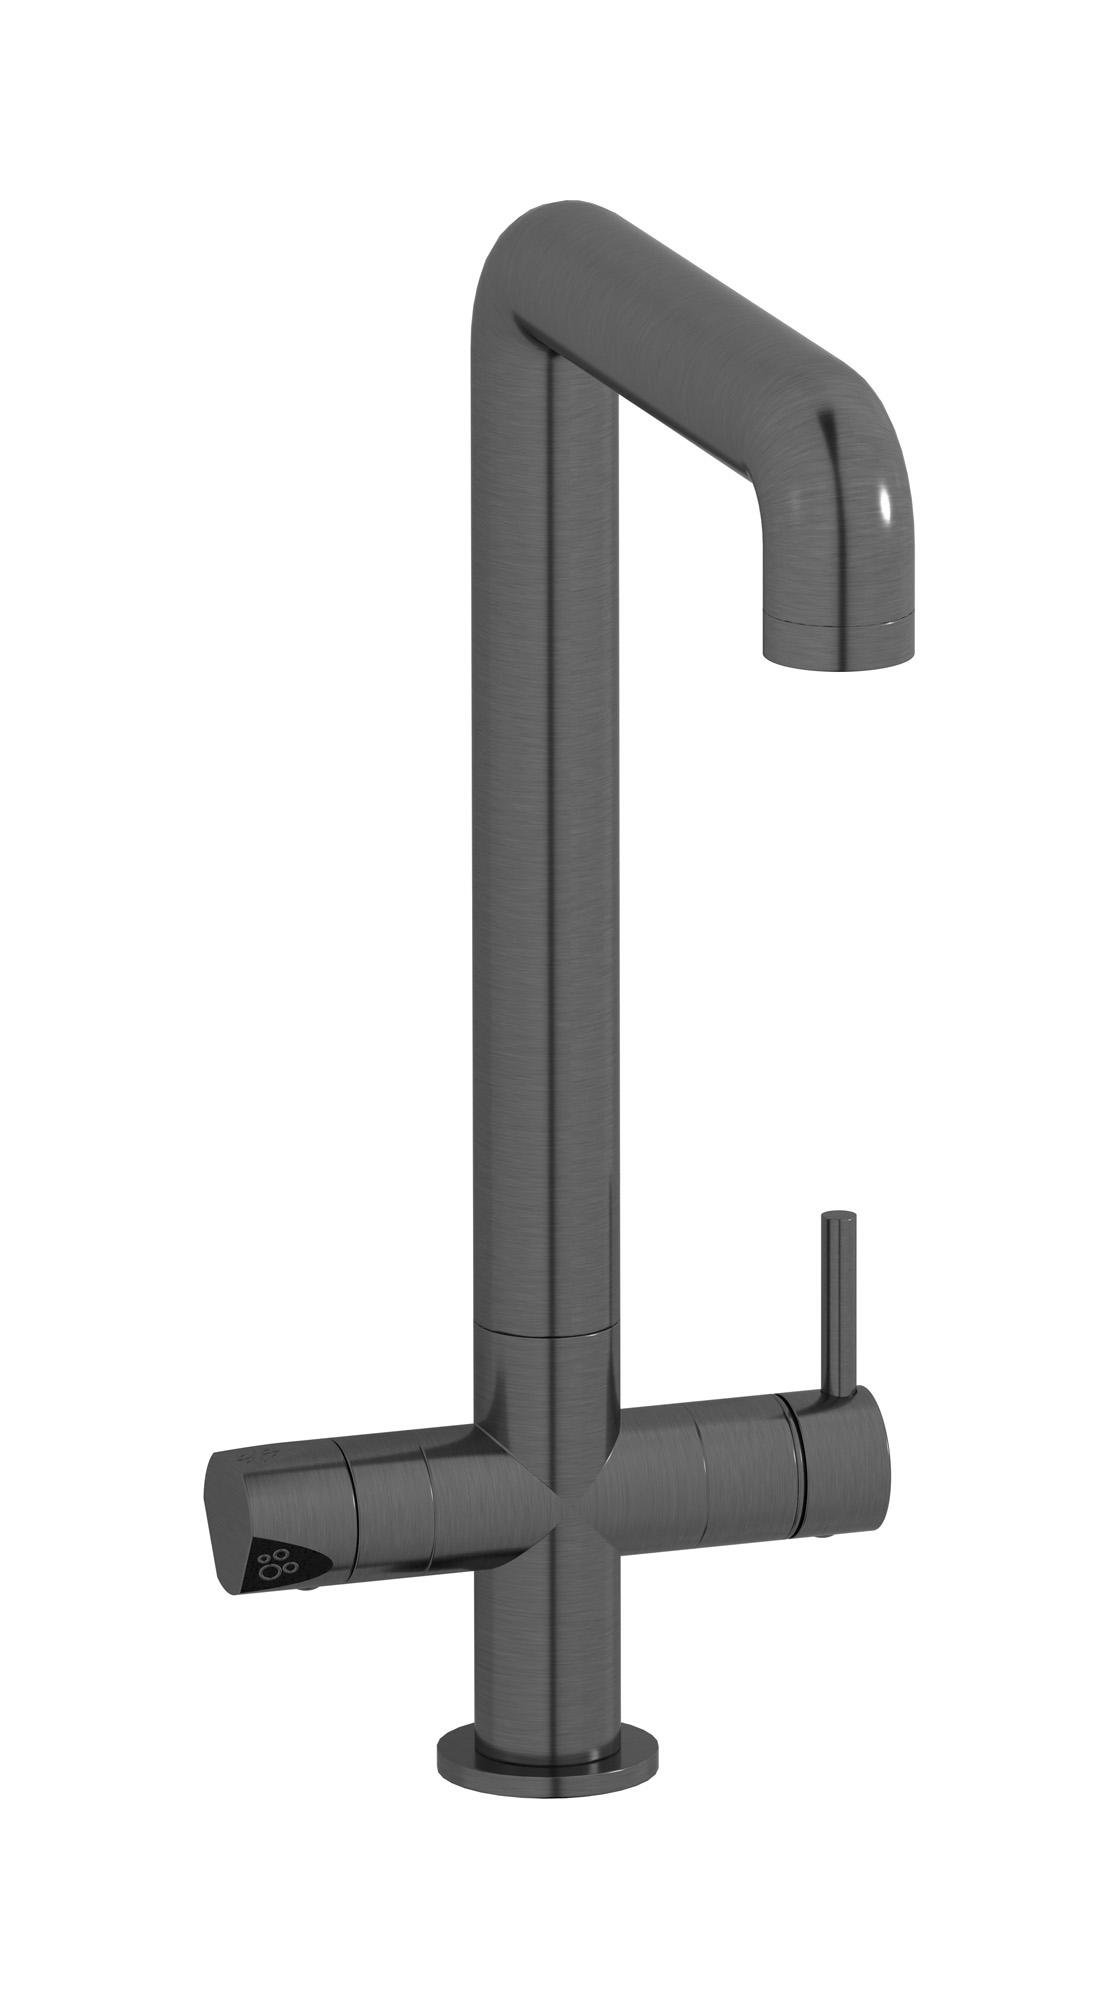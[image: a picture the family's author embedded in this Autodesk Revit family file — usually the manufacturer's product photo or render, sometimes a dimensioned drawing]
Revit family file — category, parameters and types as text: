
# Revit family: PU385
name_source: partatom
category: Apparecchi idraulici
units: mm (PartAtom-declared; Revit-internal decimal feet)

## family parameters
Basato su piano di lavoro = No
Condiviso = No
Mantieni orientamento annotazione = No
Numero OmniClass = 23.45.55.17
Punto di calcolo locali = No
Quota connettore circolare = Usa diametro
Sempre verticale = Sì
Taglio con vuoti quando caricato = No
Tipo di parte = Normale
Titolo OmniClass = Mixing Faucets

## types (6) — shared parameters
Cold water inlet = 10 mm  [stored 0.0328084 ft]
Commenti sul tipo = 4-in-1 monohole kitchen mixer for running water, natural filtered water, cold filtered and sparkling filtered water
Connessione CW = No
Connessione HW = No
Connessione di scarico = No
Connessione di ventilazione = No
Descrizione = 4-in-1 monohole kitchen mixer for running water, natural filtered water, cold filtered and sparkling filtered water
Hot water inlet = 10 mm  [stored 0.0328084 ft]
Produttore = IB Rubinetterie S.p.A.
zero-valued in all types: Prospetto di default

## per-type parameters (varying)
| type | Finishes surface | Immagine tipo | Modello |
| Chrome | IB_Chrome | PU385CC.jpg | PU385CC |
| Black chrome | IB_Black chrome | PU385CS.jpg | PU385CS |
| Pale gold | IB_Pale gold | PU385IS.jpg | PU385IS |
| Matt black | IB_matt black | PU385NP.jpg | PU385NP |
| Rose gold | IB_Rose gold | PU385RS.jpg | PU385RS |
| Brushed nickel | IB_Brushed nickel | PU385SS.jpg | PU385SS |

note: [stored X ft] marks values corroborated as IEEE doubles in the binary element streams (Revit-internal decimal feet)
